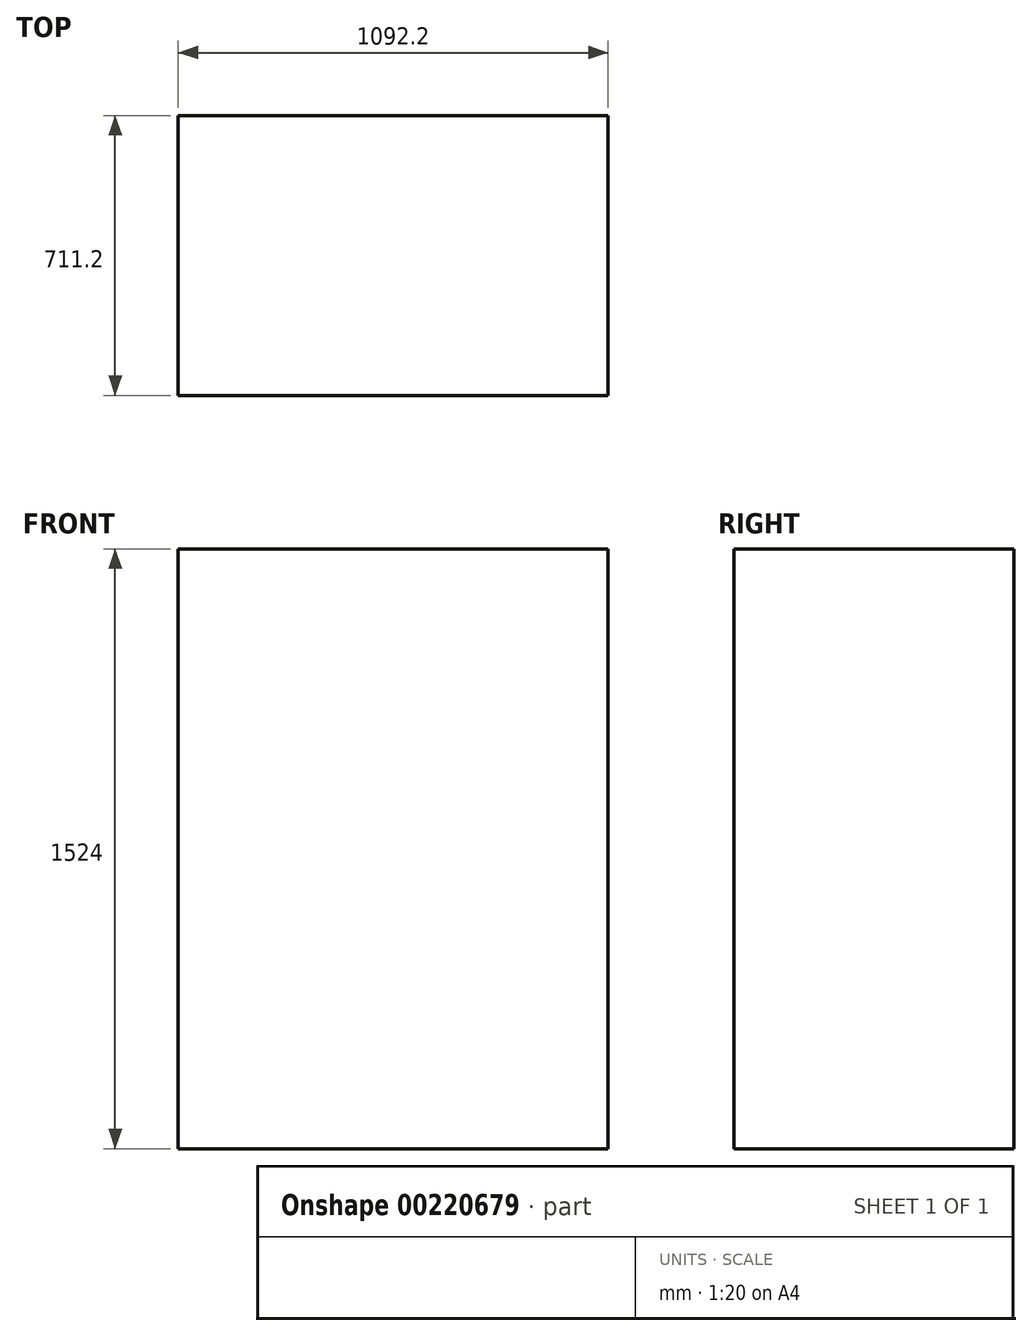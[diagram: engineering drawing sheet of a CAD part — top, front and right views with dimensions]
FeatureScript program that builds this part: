
annotation { "Feature Type Name" : "Feature", "Feature Type Description" : "" }
export const myFeature = defineFeature(function(context is Context, id is Id, definition is map)
    precondition{}
    {
        {
            var Q0;
            Q0=qCreatedBy(makeId("Top.planeOp"),FACE);
            var sketch = newSketch(context, id + "F0", { "sketchPlane" : qUnion([Q0])});
            skLineSegment(sketch, "E0.bottom", {"start": v(705.05, -345.82) * mm, "end": v(-387.15, -345.82) * mm});
            skLineSegment(sketch, "E0.top", {"start": v(705.05, 365.38) * mm, "end": v(-387.15, 365.38) * mm});
            skLineSegment(sketch, "E0.left", {"start": v(705.05, -345.82) * mm, "end": v(705.05, 365.38) * mm});
            skLineSegment(sketch, "E0.right", {"start": v(-387.15, -345.82) * mm, "end": v(-387.15, 365.38) * mm});
            skPoint(sketch, "E0.middle", {"position": v(158.95, 9.78) * mm});
            skSolve(sketch);
        }
        {
            var Q0;
            Q0 = qSketchRegion(id + "F0", true);
            extrude(context, id + "F1", {"entities" : qUnion([Q0]), "depth" : 1524 * mm});
        }
    });
